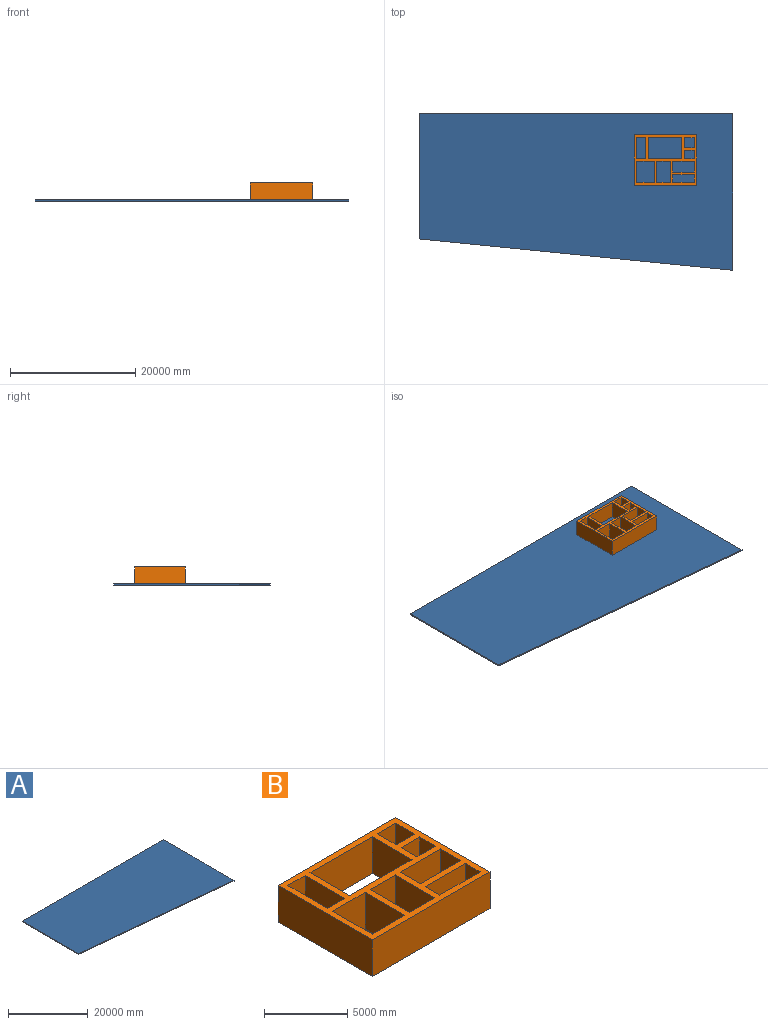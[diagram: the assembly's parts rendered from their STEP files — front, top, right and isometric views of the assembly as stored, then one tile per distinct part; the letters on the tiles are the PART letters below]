
ASSEMBLY  parts=2 mates=1
PART A: 6 faces, bbox 50000x25000x200 mm
  f0: plane 20000x200mm, normal (-1,0,0), area 4000000mm2, adj f1,f3,f4,f5
  f1: plane 50000x5000mm, normal (-0.1,-1,0), area 10049875.6mm2, adj f0,f2,f4,f5
  f2: plane 25000x200mm, normal (1,0,0), area 5000000mm2, adj f1,f3,f4,f5
  f3: plane 50000x200mm, normal (0,1,0), area 10000000mm2, adj f0,f2,f4,f5
  f4: plane 50000x25000mm, normal (0,0,1), area 1125000000mm2, adj f0,f1,f2,f3
  f5: plane 50000x25000mm, normal (0,0,-1), area 1125000000mm2, adj f0,f1,f2,f3
PART B: 38 faces, bbox 10000x8000x2700 mm
  f0: plane 2700x1707.89mm, normal (-1,0,0), area 4611304.6mm2, adj f8,f9,f20,f30
  f1: plane 2700x1344.27mm, normal (-1,0,0), area 3629537.2mm2, adj f8,f9,f23,f26
  f2: plane 2700x1242.11mm, normal (-1,0,0), area 3353695.4mm2, adj f8,f9,f17,f29
  f3: plane 5292.86x2700mm, normal (0,-1,0), area 14290720.4mm2, adj f8,f9,f25,f35
  f4: plane 2700x1456.61mm, normal (0,-1,0), area 3932835.6mm2, adj f8,f9,f16,f34
  f5: plane 3370x2700mm, normal (1,0,0), area 9099000mm2, adj f7,f8,f9,f22
  f6: plane 2700x2136.39mm, normal (0,1,0), area 5768256.8mm2, adj f8,f9,f32,f37
  f7: plane 2770.63x2700mm, normal (0,1,0), area 7480699.1mm2, adj f5,f8,f9,f36
  f8: plane 10000x8000mm, normal (0,0,1), area 26016275.9mm2, adj f0,f1,f2,f3,f4,f5,f6,f7
  f9: plane 10000x8000mm, normal (0,0,-1), area 26016275.9mm2, adj f0,f1,f2,f3,f4,f5,f6,f7
  f10: plane 8000x2700mm, normal (1,0,0), area 21600000mm2, adj f8,f9,f11,f13
  f11: plane 10000x2700mm, normal (0,1,0), area 27000000mm2, adj f8,f9,f10,f12
  f12: plane 8000x2700mm, normal (-1,0,0), area 21600000mm2, adj f8,f9,f11,f13
  f13: plane 10000x2700mm, normal (0,-1,0), area 27000000mm2, adj f8,f9,f10,f12
  f14: plane 2700x1605.73mm, normal (-1,0,0), area 4335462.8mm2, adj f8,f9,f15,f27
  f15: plane 2700x1570.54mm, normal (0,-1,0), area 4240444mm2, adj f8,f9,f14,f28
  f16: plane 3370x2700mm, normal (1,0,0), area 9099000mm2, adj f4,f8,f9,f21
  f17: plane 3412.98x2700mm, normal (0,1,0), area 9215044.1mm2, adj f2,f8,f9,f33
  f18: plane 2700x2136.39mm, normal (0,-1,0), area 5768256.8mm2, adj f8,f9,f32,f37
  f19: plane 5292.86x2700mm, normal (0,1,0), area 14290720.4mm2, adj f8,f9,f25,f35
  f20: plane 3412.98x2700mm, normal (0,-1,0), area 9215044.1mm2, adj f0,f8,f9,f31
  f21: plane 2700x1456.61mm, normal (0,1,0), area 3932835.6mm2, adj f8,f9,f16,f34
  f22: plane 2770.63x2700mm, normal (0,-1,0), area 7480699.1mm2, adj f5,f8,f9,f36
  f23: plane 2700x1570.54mm, normal (0,1,0), area 4240444mm2, adj f1,f8,f9,f24
  f24: plane 2700x1344.27mm, normal (1,0,0), area 3629537.2mm2, adj f8,f9,f23,f26
  f25: plane 3370x2700mm, normal (-1,0,0), area 9099000mm2, adj f3,f8,f9,f19
  f26: plane 2700x1570.54mm, normal (0,-1,0), area 4240444mm2, adj f1,f8,f9,f24
  f27: plane 2700x1570.54mm, normal (0,1,0), area 4240444mm2, adj f8,f9,f14,f28
  f28: plane 2700x1605.73mm, normal (1,0,0), area 4335462.8mm2, adj f8,f9,f15,f27
  f29: plane 3412.98x2700mm, normal (0,-1,0), area 9215044.1mm2, adj f2,f8,f9,f33
  f30: plane 3412.98x2700mm, normal (0,1,0), area 9215044.1mm2, adj f0,f8,f9,f31
  f31: plane 2700x1707.89mm, normal (1,0,0), area 4611304.6mm2, adj f8,f9,f20,f30
  f32: plane 3370x2700mm, normal (-1,0,0), area 9099000mm2, adj f6,f8,f9,f18
  f33: plane 2700x1242.11mm, normal (1,0,0), area 3353695.4mm2, adj f8,f9,f17,f29
  f34: plane 3370x2700mm, normal (-1,0,0), area 9099000mm2, adj f4,f8,f9,f21
  f35: plane 3370x2700mm, normal (1,0,0), area 9099000mm2, adj f3,f8,f9,f19
  f36: plane 3370x2700mm, normal (-1,0,0), area 9099000mm2, adj f7,f8,f9,f22
  f37: plane 3370x2700mm, normal (1,0,0), area 9099000mm2, adj f6,f8,f9,f18
PLACE A at identity fixed
PLACE B t=(39303.02,12606.18,200)mm
MATE planar B.f9 <-> A.f4  axis (0,0,-1) through (39516.41,12533.67,200)mm
